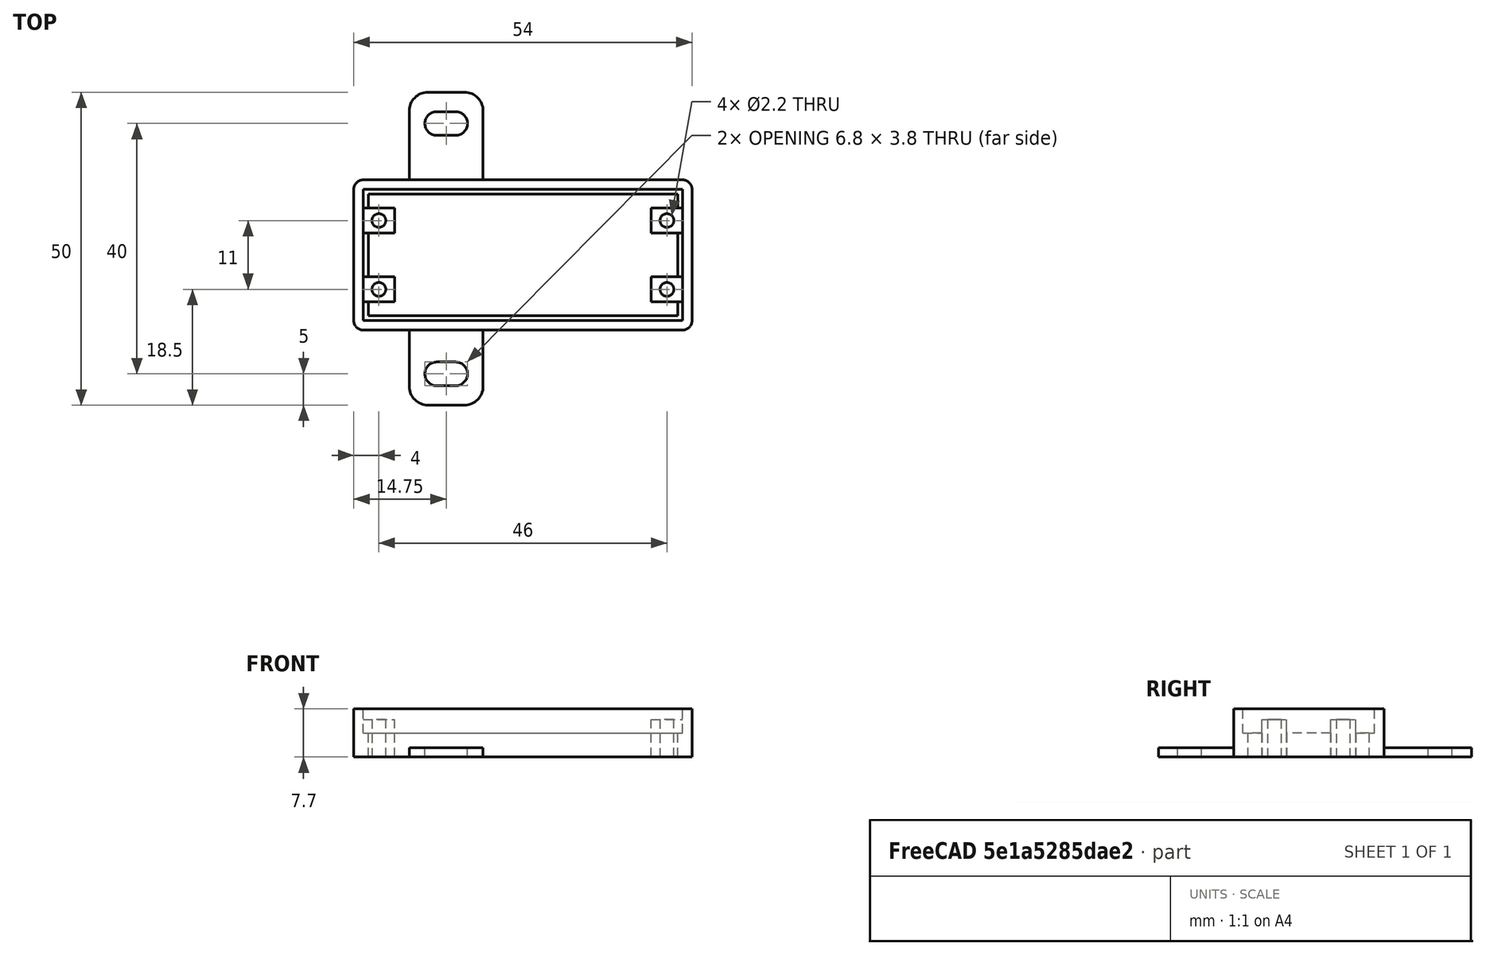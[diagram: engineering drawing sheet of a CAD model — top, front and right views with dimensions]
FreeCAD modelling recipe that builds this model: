
FCSTD DOCUMENT  (FreeCAD 0.21R33694 (Git))
Label: 4corner_offset_holes
License: All rights reserved
LicenseURL: http://en.wikipedia.org/wiki/All_rights_reserved
objects: Part::Box×4, Part::MultiFuse×3, Part::FeaturePython×2, Part::Cut×2, Spreadsheet::Sheet×1, Part::Cylinder×1, Part::Fillet×1, Part::Feature×1, App::Part×1
note: 14 computed .brp shape members not serialized (recipe doc carries the construction recipe); baked Part::Feature solids carry a one-line shape summary decoded from their .brp

FEATURE [Spreadsheet::Sheet] Spreadsheet  label="p"
  cells = A1='hole_x_dist; B1(hole_x_dist)=46; A2='hole_y_dist; B2(hole_y_dist)=11; A3='pcb_under; B3(pcb_under)=3; A4='pcb_x; B4(pcb_x)=51; A5='pcb_y; B5(pcb_y)=21; A6='hole_stand_x; B6(hole_stand_x)=5; A7='hole_stand_x_offset; B7(hole_stand_x_offset)=0; A8='hole_stand_y; B8(hole_stand_y)=4; A9='hole_stand_y_offset; B9(hole_stand_y_offset)=3; A10='hole_r; B10(hole_r)=1.1; A11='box_wall; B11(box_wall)=1.5; A12='under_layer; B12(under_layer)=3; A13='pcb_height; B13(pcb_height)=1.7; A14='under_pcb_border; B14(under_pcb_border)=0.8
FEATURE [Part::Box] Box  label="bottom cube"
  AttacherType = Attacher::AttachEngine3D
  Height = 7.7
  Length = 54
  Width = 24
  expr: Height = <<p>>.pcb_under + <<p>>.pcb_height + <<p>>.under_layer
  expr: Length = <<p>>.pcb_x + <<p>>.box_wall * 2
  expr: Width = <<p>>.pcb_y + <<p>>.box_wall * 2
FEATURE [Part::Box] Box001  label="bottom extraction"
  AttacherType = Attacher::AttachEngine3D
  Height = 10
  Length = 49.4
  Placement = pos=(2.3,2.3,0) rot=(0,0,1;0rad)
  Width = 19.4
  expr: .Placement.Base.x = <<p>>.under_pcb_border + <<p>>.box_wall
  expr: .Placement.Base.y = <<p>>.under_pcb_border + <<p>>.box_wall
  expr: Length = <<p>>.pcb_x - <<p>>.under_pcb_border * 2
  expr: Width = <<p>>.pcb_y - <<p>>.under_pcb_border * 2
FEATURE [Part::Box] Box002  label="pcb extraction"
  AttacherType = Attacher::AttachEngine3D
  Height = 10
  Length = 51
  Placement = pos=(1.5,1.5,3.8) rot=(0,0,1;0rad)
  Width = 21
  expr: .Placement.Base.x = <<p>>.box_wall
  expr: .Placement.Base.y = <<p>>.box_wall
  expr: .Placement.Base.z = <<p>>.under_pcb_border + <<p>>.under_layer
  expr: Length = <<p>>.pcb_x
  expr: Width = <<p>>.pcb_y
FEATURE [Part::MultiFuse] Fusion  label="bottom extraction001"
  Shapes = -> [Box001,Box002]
FEATURE [Part::Box] Box003  label="hole stand cube"
  AttacherType = Attacher::AttachEngine3D
  Height = 6
  Length = 5
  Placement = pos=(1.5,4.5,0) rot=(0,0,1;0rad)
  Width = 4
  expr: .Placement.Base.x = <<p>>.box_wall + <<p>>.hole_stand_x_offset
  expr: .Placement.Base.y = <<p>>.box_wall + <<p>>.hole_stand_y_offset
  expr: Height = <<p>>.pcb_under + <<p>>.under_layer
  expr: Length = <<p>>.hole_stand_x
  expr: Width = <<p>>.hole_stand_y
FEATURE [Part::FeaturePython] Array  label="hole stand array"  # Draft array (typed FeaturePython)
  Angle = 360
  ArrayType = 0
  Axis = (0,0,1)
  Base = -> Box003
  Center = (0,0,0)
  Count = 4
  Fuse = false
  IntervalAxis = (0,0,0)
  IntervalX = (46,0,0)
  IntervalY = (0,11,0)
  IntervalZ = (0,0,1)
  NumberPolar = 1
  NumberX = 2
  NumberY = 2
  NumberZ = 1
  expr: .IntervalX.x = <<p>>.pcb_x - <<p>>.hole_stand_x - 2 * <<p>>.hole_stand_x_offset
  expr: .IntervalY.y = <<p>>.pcb_y - <<p>>.hole_stand_y - 2 * <<p>>.hole_stand_y_offset
FEATURE [Part::Cylinder] Cylinder  label="pcb hole"
  Angle = 360
  AttacherType = Attacher::AttachEngine3D
  FirstAngle = 0
  Height = 10
  Placement = pos=(4,6.5,0) rot=(0,0,1;0rad)
  Radius = 1.1
  SecondAngle = 0
  expr: .Placement.Base.x = (<<p>>.box_wall * 2 + <<p>>.pcb_x - <<p>>.hole_x_dist) / 2
  expr: .Placement.Base.y = (<<p>>.box_wall * 2 + <<p>>.pcb_y - <<p>>.hole_y_dist) / 2
  expr: Radius = <<p>>.hole_r
FEATURE [Part::FeaturePython] Array001  label="hole array"  # Draft array (typed FeaturePython)
  Angle = 360
  ArrayType = 0
  Axis = (0,0,1)
  Base = -> Cylinder
  Center = (0,0,0)
  Count = 4
  Fuse = false
  IntervalAxis = (0,0,0)
  IntervalX = (46,0,0)
  IntervalY = (0,11,0)
  IntervalZ = (0,0,1)
  NumberPolar = 1
  NumberX = 2
  NumberY = 2
  NumberZ = 1
  expr: .IntervalX.x = <<p>>.hole_x_dist
  expr: .IntervalY.y = <<p>>.hole_y_dist
FEATURE [Part::Fillet] Fillet001  label="bottom cube fillet"
  Base = -> Box
  Edges = 4 edges r=1.5: [Edge1,Edge3,Edge5,Edge7]
FEATURE [Part::Feature] Cut002001  label="attach plane y dir001"
  Placement = pos=(8.85,-12,0) rot=(0,0,1;0rad)
  shape: bbox 11.8 x 50 x 1.5 mm, 20 faces (baked)
FEATURE [Part::MultiFuse] Fusion002  label="bottom fusion"
  Shapes = -> [Fillet001,Cut002001]
FEATURE [Part::Cut] Cut  label="pcb box cut"
  Base = -> Fusion002
  Tool = -> Fusion
FEATURE [Part::MultiFuse] Fusion001  label="frame fusion"
  Shapes = -> [Array,Cut]
FEATURE [Part::Cut] Cut001  label="frame fusion with holes"
  Base = -> Fusion001
  Tool = -> Array001
FEATURE [App::Part] Part  label="pcb with 4 holes part"
  Group = -> [Fusion,Fusion002,Box002,Box003,Box001,Array001,Cut,Array,Cylinder,Fusion001,Cut001]
  Origin = -> Origin
